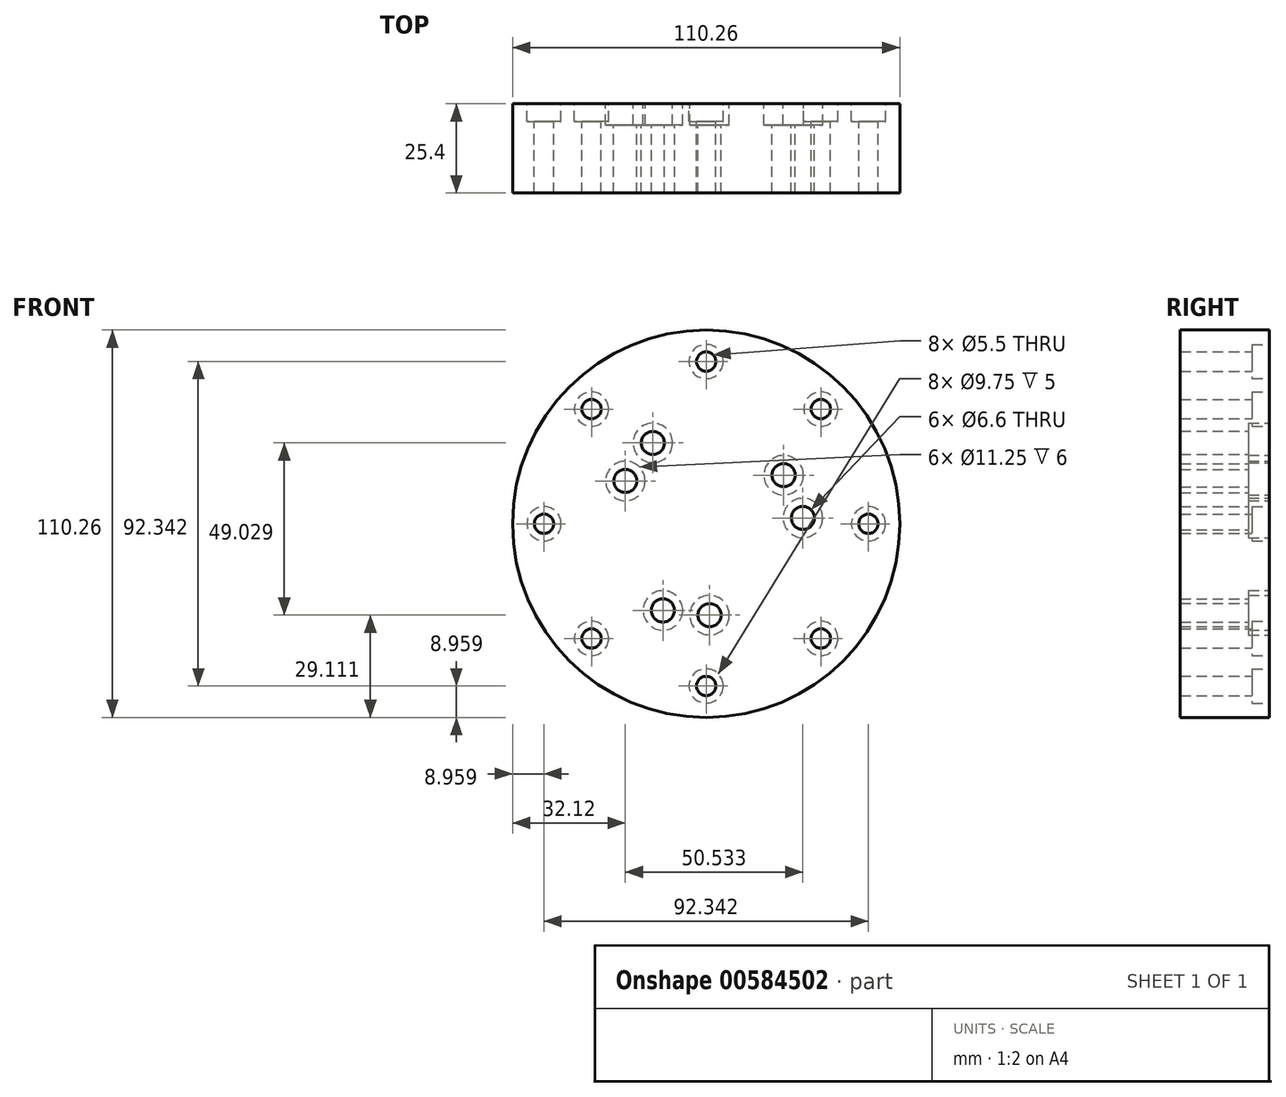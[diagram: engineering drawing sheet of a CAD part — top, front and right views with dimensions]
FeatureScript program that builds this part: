
annotation { "Feature Type Name" : "Feature", "Feature Type Description" : "" }
export const myFeature = defineFeature(function(context is Context, id is Id, definition is map)
    precondition{}
    {
        {
            var Q0;
            Q0=qCreatedBy(makeId("Front.planeOp"),FACE);
            var sketch = newSketch(context, id + "F0", { "sketchPlane" : qUnion([Q0])});
            skCircle(sketch, "E0", {"center": v(0, 0) * mm, "radius": 55.13 * mm});
            skPoint(sketch, "E1", {"position": v(0, 46.17) * mm});
            skPoint(sketch, "E2.1.0", {"position": v(-32.65, 32.65) * mm});
            skPoint(sketch, "E2.2.0", {"position": v(-46.17, 0) * mm});
            skPoint(sketch, "E2.3.0", {"position": v(-32.65, -32.65) * mm});
            skPoint(sketch, "E2.4.0", {"position": v(0, -46.17) * mm});
            skPoint(sketch, "E2.5.0", {"position": v(32.65, -32.65) * mm});
            skPoint(sketch, "E2.6.0", {"position": v(46.17, 0) * mm});
            skPoint(sketch, "E2.7.0", {"position": v(32.65, 32.65) * mm});
            skSolve(sketch);
        }
        {
            var Q0;
            Q0=makeQuery(id+"F0.imprint","IMPRINT",FACE,{"disambiguationData":[TD([[makeQuery(id+"F0.imprint","IMPRINT",EDGE,{"derivedFrom":sQuery(id+"F0.wireOp",EDGE,"E0")}),1.0]])]});
            var sketch = newSketch(context, id + "F1", { "sketchPlane" : qUnion([Q0])});
            skPoint(sketch, "E3", {"position": v(-23.01, 12.18) * mm});
            skPoint(sketch, "E4", {"position": v(-15.19, 23.01) * mm});
            skPoint(sketch, "E5.1.0", {"position": v(-12.33, -24.66) * mm});
            skPoint(sketch, "E5.1.1", {"position": v(0.96, -26.02) * mm});
            skPoint(sketch, "E5.2.0", {"position": v(27.52, 1.65) * mm});
            skPoint(sketch, "E5.2.1", {"position": v(22.06, 13.84) * mm});
            skPoint(sketch, "E5.center", {"position": v(0, 0) * mm});
            skSolve(sketch);
        }
        {
            var Q0;
            Q0=makeQuery(id+"F0.imprint","IMPRINT",FACE,{"disambiguationData":[TD([[makeQuery(id+"F0.imprint","IMPRINT",EDGE,{"derivedFrom":sQuery(id+"F0.wireOp",EDGE,"E0")}),1.0]])]});
            extrude(context, id + "F2", {"entities" : qUnion([Q0]), "depth" : 25.4 * mm, "offsetDistance" : 25.4 * mm});
        }
        {
            var Q0;
            Q0=sQuery(id+"F0.wireOp",VERTEX,"E2.1.0");
            var Q1;
            Q1=sQuery(id+"F0.wireOp",VERTEX,"E1");
            var Q2;
            Q2=sQuery(id+"F0.wireOp",VERTEX,"E2.7.0");
            var Q3;
            Q3=sQuery(id+"F0.wireOp",VERTEX,"E2.6.0");
            var Q4;
            Q4=sQuery(id+"F0.wireOp",VERTEX,"E2.5.0");
            var Q5;
            Q5=sQuery(id+"F0.wireOp",VERTEX,"E2.4.0");
            var Q6;
            Q6=sQuery(id+"F0.wireOp",VERTEX,"E2.2.0");
            var Q7;
            Q7=sQuery(id+"F0.wireOp",VERTEX,"E2.3.0");
            var Q8;
            Q8=makeQuery(id+"F2.opExtrude","SWEPT_BODY",BODY,{"disambiguationData":[OSD([sQuery(id+"F0.wireOp",EDGE,"E0")])]});
            hole(context, id + "F3", {"style" : HoleStyle.C_BORE, "endStyle" : HoleEndStyle.THROUGH, "oppositeDirection" : true, "standardTappedOrClearance" : lookupTablePath({ "standard" : "ISO", "fit" : "Normal", "size" : "M5", "type" : "Clearance" }), "standardBlindInLast" : lookupTablePath({ "fit" : "Standard", "standard" : "ISO", "size" : "M5", "type" : "Clearance" }), "holeDiameter" : 5.5 * mm, "cBoreDiameter" : 9.75 * mm, "cBoreDepth" : 5 * mm, "majorDiameter" : 6.35 * mm, "isTappedThrough" : true, "tappedDepth" : 12.7 * mm, "tapClearance" : 3, "startFromSketch" : true, "locations" : qUnion([Q0, Q1, Q2, Q3, Q4, Q5, Q6, Q7]), "scope" : qUnion([Q8])});
        }
        {
            var Q0;
            Q0=sQuery(id+"F1.wireOp",VERTEX,"E5.1.0");
            var Q1;
            Q1=sQuery(id+"F1.wireOp",VERTEX,"E5.1.1");
            var Q2;
            Q2=sQuery(id+"F1.wireOp",VERTEX,"E3");
            var Q3;
            Q3=sQuery(id+"F1.wireOp",VERTEX,"E4");
            var Q4;
            Q4=sQuery(id+"F1.wireOp",VERTEX,"E5.2.1");
            var Q5;
            Q5=sQuery(id+"F1.wireOp",VERTEX,"E5.2.0");
            var Q6;
            Q6=makeQuery(id+"F2.opExtrude","SWEPT_BODY",BODY,{"disambiguationData":[OSD([sQuery(id+"F0.wireOp",EDGE,"E0")])]});
            hole(context, id + "F4", {"style" : HoleStyle.C_BORE, "endStyle" : HoleEndStyle.THROUGH, "oppositeDirection" : true, "standardTappedOrClearance" : lookupTablePath({ "standard" : "ISO", "fit" : "Normal", "size" : "M6", "type" : "Clearance" }), "standardBlindInLast" : lookupTablePath({ "fit" : "Standard", "standard" : "ISO", "size" : "M6", "type" : "Clearance" }), "holeDiameter" : 6.6 * mm, "cBoreDiameter" : 11.25 * mm, "cBoreDepth" : 6 * mm, "majorDiameter" : 6.35 * mm, "isTappedThrough" : true, "tappedDepth" : 12.7 * mm, "tapClearance" : 3, "startFromSketch" : true, "locations" : qUnion([Q0, Q1, Q2, Q3, Q4, Q5]), "scope" : qUnion([Q6])});
        }
    });
